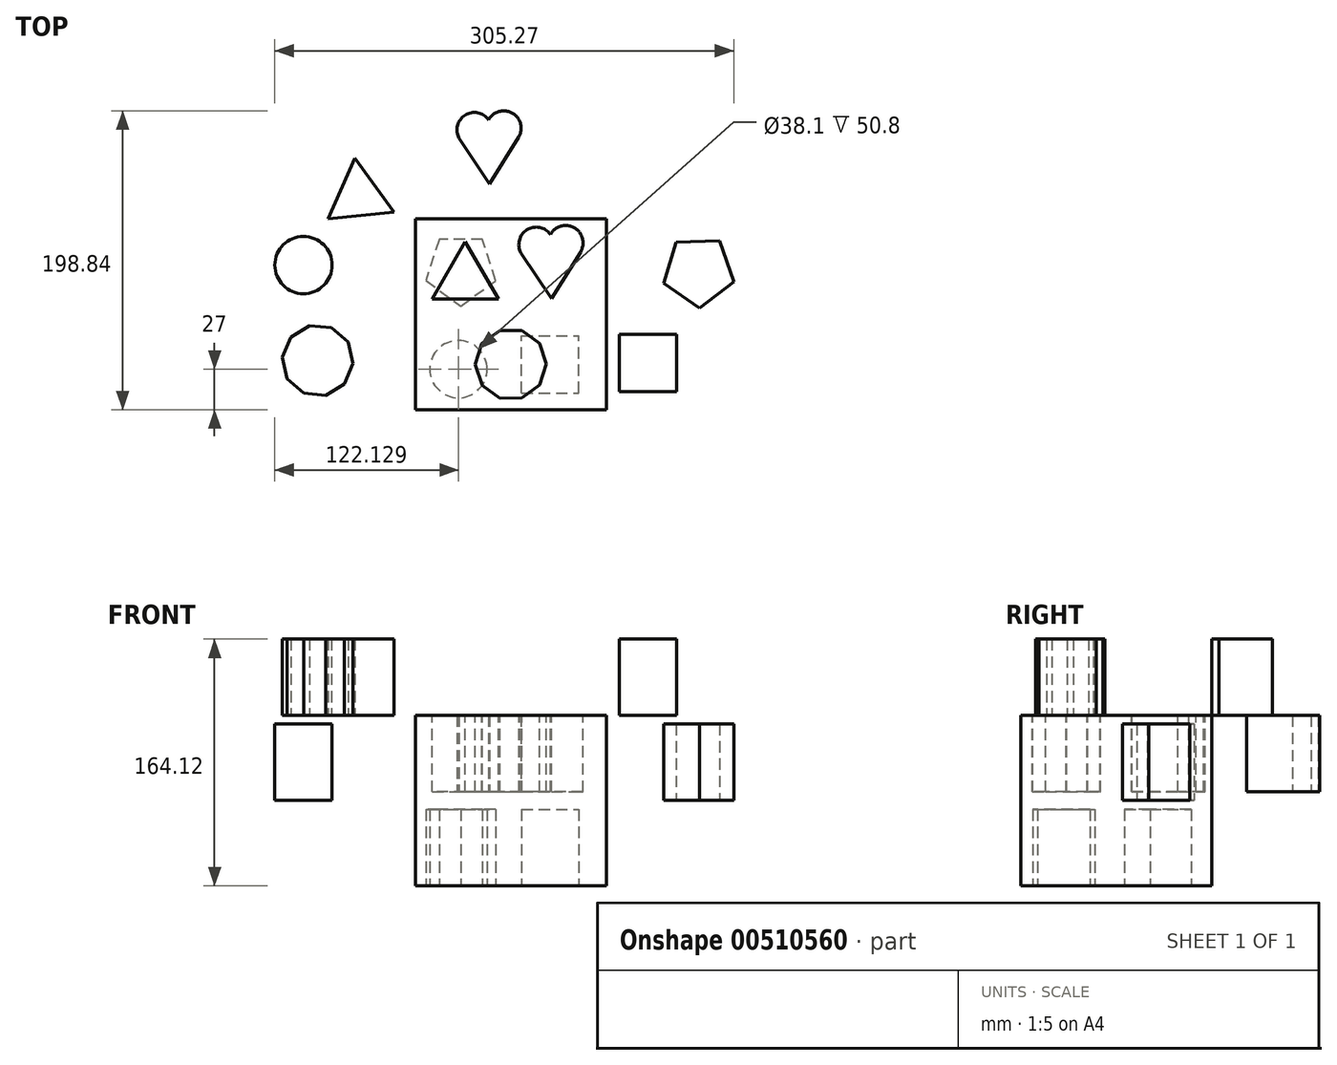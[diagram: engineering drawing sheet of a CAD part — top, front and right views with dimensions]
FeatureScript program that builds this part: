
annotation { "Feature Type Name" : "Feature", "Feature Type Description" : "" }
export const myFeature = defineFeature(function(context is Context, id is Id, definition is map)
    precondition{}
    {
        {
            var Q0;
            Q0=qCreatedBy(makeId("Front.planeOp"),FACE);
            var sketch = newSketch(context, id + "F0", { "sketchPlane" : qUnion([Q0])});
            skLineSegment(sketch, "E0.bottom", {"start": v(-63.3, 56.37) * mm, "end": v(63.7, 56.37) * mm});
            skLineSegment(sketch, "E0.top", {"start": v(-63.3, -56.95) * mm, "end": v(63.7, -56.95) * mm});
            skLineSegment(sketch, "E0.left", {"start": v(-63.3, 56.37) * mm, "end": v(-63.3, -56.95) * mm});
            skLineSegment(sketch, "E0.right", {"start": v(63.7, 56.37) * mm, "end": v(63.7, -56.95) * mm});
            skSolve(sketch);
        }
        {
            var Q0;
            Q0 = qSketchRegion(id + "F0", true);
            extrude(context, id + "F1", {"entities" : qUnion([Q0]), "depth" : 127 * mm});
        }
        {
            var Q0;
            Q0=makeQuery(id+"F1.opExtrude","SWEPT_FACE",FACE,{"disambiguationData":[OSD([sQuery(id+"F0.wireOp",EDGE,"E0.top")])]});
            var sketch = newSketch(context, id + "F2", { "sketchPlane" : qUnion([Q0])});
            skCircle(sketch, "E1", {"center": v(-34.88, 100) * mm, "radius": 19.05 * mm});
            skSolve(sketch);
        }
        {
            var Q0;
            Q0=makeQuery(id+"F2.imprint","IMPRINT",FACE,{"disambiguationData":[TD([[makeQuery(id+"F2.imprint","IMPRINT",EDGE,{"derivedFrom":sQuery(id+"F2.wireOp",EDGE,"E1")}),1.0]])]});
            extrude(context, id + "F3", {"entities" : qUnion([Q0]), "operationType" : NewBodyOperationType.REMOVE, "oppositeDirection" : true, "depth" : 50.8 * mm});
        }
        {
            var Q0;
            Q0=makeQuery(id+"F1.opExtrude","SWEPT_FACE",FACE,{"disambiguationData":[OSD([sQuery(id+"F0.wireOp",EDGE,"E0.top")])]});
            var sketch = newSketch(context, id + "F4", { "sketchPlane" : qUnion([Q0])});
            skLineSegment(sketch, "E2.bottom", {"start": v(7.05, 115.87) * mm, "end": v(45.15, 115.87) * mm});
            skLineSegment(sketch, "E2.top", {"start": v(7.05, 77.77) * mm, "end": v(45.15, 77.77) * mm});
            skLineSegment(sketch, "E2.left", {"start": v(7.05, 115.87) * mm, "end": v(7.05, 77.77) * mm});
            skLineSegment(sketch, "E2.right", {"start": v(45.15, 115.87) * mm, "end": v(45.15, 77.77) * mm});
            skSolve(sketch);
        }
        {
            var Q0;
            Q0=makeQuery(id+"F4.imprint","IMPRINT",FACE,{"disambiguationData":[TD([[makeQuery(id+"F4.imprint","IMPRINT",EDGE,{"derivedFrom":sQuery(id+"F4.wireOp",EDGE,"E2.bottom")}),-1.0]])]});
            extrude(context, id + "F5", {"entities" : qUnion([Q0]), "operationType" : NewBodyOperationType.REMOVE, "oppositeDirection" : true, "depth" : 50.8 * mm});
        }
        {
            var Q0;
            Q0=makeQuery(id+"F1.opExtrude","SWEPT_FACE",FACE,{"disambiguationData":[OSD([sQuery(id+"F0.wireOp",EDGE,"E0.top")])]});
            var sketch = newSketch(context, id + "F6", { "sketchPlane" : qUnion([Q0])});
            skCircle(sketch, "E3.cCircle", {"center": v(-33.35, 33.53) * mm, "radius": 19.77 * mm, "construction": true});
            skLineSegment(sketch, "E3.0", {"start": v(-47.68, 13.73) * mm, "end": v(-56.6, 41.05) * mm});
            skLineSegment(sketch, "E3.1", {"start": v(-56.6, 41.05) * mm, "end": v(-33.38, 57.97) * mm});
            skLineSegment(sketch, "E3.2", {"start": v(-33.38, 57.97) * mm, "end": v(-10.11, 41.12) * mm});
            skLineSegment(sketch, "E3.3", {"start": v(-10.11, 41.12) * mm, "end": v(-18.95, 13.78) * mm});
            skLineSegment(sketch, "E3.4", {"start": v(-18.95, 13.78) * mm, "end": v(-47.68, 13.73) * mm});
            skPoint(sketch, "E3.0.midPoint", {"position": v(-52.14, 27.39) * mm});
            skSolve(sketch);
        }
        {
            var Q0;
            Q0=makeQuery(id+"F6.imprint","IMPRINT",FACE,{"disambiguationData":[TD([[makeQuery(id+"F6.imprint","IMPRINT",EDGE,{"derivedFrom":sQuery(id+"F6.wireOp",EDGE,"E3.0")}),-1.0]])]});
            extrude(context, id + "F7", {"entities" : qUnion([Q0]), "operationType" : NewBodyOperationType.REMOVE, "oppositeDirection" : true, "depth" : 50.8 * mm});
        }
        {
            var Q0;
            Q0=makeQuery(id+"F1.opExtrude","SWEPT_FACE",FACE,{"disambiguationData":[OSD([sQuery(id+"F0.wireOp",EDGE,"E0.bottom")])]});
            var sketch = newSketch(context, id + "F8", { "sketchPlane" : qUnion([Q0])});
            skLineSegment(sketch, "E4", {"start": v(-30.32, -15.29) * mm, "end": v(-52.34, -53.43) * mm});
            skLineSegment(sketch, "E5", {"start": v(-52.34, -53.43) * mm, "end": v(-8.3, -53.43) * mm});
            skLineSegment(sketch, "E6", {"start": v(-8.3, -53.43) * mm, "end": v(-30.32, -15.29) * mm});
            skSolve(sketch);
        }
        {
            var Q0;
            Q0 = qSketchRegion(id + "F8", true);
            extrude(context, id + "F9", {"entities" : qUnion([Q0]), "operationType" : NewBodyOperationType.REMOVE, "oppositeDirection" : true, "depth" : 50.8 * mm});
        }
        {
            var Q0;
            Q0=makeQuery(id+"F1.opExtrude","SWEPT_FACE",FACE,{"disambiguationData":[OSD([sQuery(id+"F0.wireOp",EDGE,"E0.bottom")])]});
            var sketch = newSketch(context, id + "F10", { "sketchPlane" : qUnion([Q0])});
            skLineSegment(sketch, "E7", {"start": v(6.74, -22.72) * mm, "end": v(26.99, -53.15) * mm});
            skLineSegment(sketch, "E8", {"start": v(26.99, -53.15) * mm, "end": v(46.25, -22.08) * mm});
            skArc(sketch, "E9", {"start": v(26.28, -10.36) * mm, "mid": v(10.67, -7.3) * mm, "end": v(6.74, -22.72) * mm});
            skArc(sketch, "E10", {"start": v(46.25, -22.08) * mm, "mid": v(42.27, -6) * mm, "end": v(26.28, -10.36) * mm});
            skPoint(sketch, "E11.orphan", {"position": v(26.99, -22.72) * mm});
            skSolve(sketch);
        }
        {
            var Q0;
            Q0=makeQuery(id+"F10.imprint","IMPRINT",FACE,{"disambiguationData":[TD([[makeQuery(id+"F10.imprint","IMPRINT",EDGE,{"derivedFrom":sQuery(id+"F10.wireOp",EDGE,"E7")}),1.0]])]});
            extrude(context, id + "F11", {"entities" : qUnion([Q0]), "operationType" : NewBodyOperationType.REMOVE, "oppositeDirection" : true, "depth" : 50.8 * mm});
        }
        {
            var Q0;
            Q0=makeQuery(id+"F1.opExtrude","SWEPT_FACE",FACE,{"disambiguationData":[OSD([sQuery(id+"F0.wireOp",EDGE,"E0.bottom")])]});
            var sketch = newSketch(context, id + "F12", { "sketchPlane" : qUnion([Q0])});
            skCircle(sketch, "E12.cCircle", {"center": v(0, -96.69) * mm, "radius": 22.53 * mm, "construction": true});
            skLineSegment(sketch, "E12.0", {"start": v(7.25, -74.14) * mm, "end": v(19.13, -82.7) * mm});
            skLineSegment(sketch, "E12.1", {"start": v(19.13, -82.7) * mm, "end": v(23.7, -96.62) * mm});
            skLineSegment(sketch, "E12.2", {"start": v(23.7, -96.62) * mm, "end": v(19.2, -110.56) * mm});
            skLineSegment(sketch, "E12.3", {"start": v(19.2, -110.56) * mm, "end": v(7.39, -119.2) * mm});
            skLineSegment(sketch, "E12.4", {"start": v(7.39, -119.2) * mm, "end": v(-7.25, -119.24) * mm});
            skLineSegment(sketch, "E12.5", {"start": v(-7.25, -119.24) * mm, "end": v(-19.13, -110.67) * mm});
            skLineSegment(sketch, "E12.6", {"start": v(-19.13, -110.67) * mm, "end": v(-23.7, -96.76) * mm});
            skLineSegment(sketch, "E12.7", {"start": v(-23.7, -96.76) * mm, "end": v(-19.2, -82.82) * mm});
            skLineSegment(sketch, "E12.8", {"start": v(-19.2, -82.82) * mm, "end": v(-7.39, -74.18) * mm});
            skLineSegment(sketch, "E12.9", {"start": v(-7.39, -74.18) * mm, "end": v(7.25, -74.14) * mm});
            skPoint(sketch, "E12.0.midPoint", {"position": v(13.19, -78.42) * mm});
            skSolve(sketch);
        }
        {
            var Q0;
            Q0=makeQuery(id+"F12.imprint","IMPRINT",FACE,{"disambiguationData":[TD([[makeQuery(id+"F12.imprint","IMPRINT",EDGE,{"derivedFrom":sQuery(id+"F12.wireOp",EDGE,"E12.0")}),-1.0]])]});
            extrude(context, id + "F13", {"entities" : qUnion([Q0]), "operationType" : NewBodyOperationType.REMOVE, "oppositeDirection" : true, "depth" : 50.8 * mm});
        }
        {
            var Q0;
            Q0=makeQuery(id+"F1.opExtrude","SWEPT_FACE",FACE,{"disambiguationData":[OSD([sQuery(id+"F0.wireOp",EDGE,"E0.bottom")])]});
            var sketch = newSketch(context, id + "F14", { "sketchPlane" : qUnion([Q0])});
            skLineSegment(sketch, "E13.bottom", {"start": v(72.05, -115.02) * mm, "end": v(110.15, -115.02) * mm});
            skLineSegment(sketch, "E13.top", {"start": v(72.05, -76.92) * mm, "end": v(110.15, -76.92) * mm});
            skLineSegment(sketch, "E13.left", {"start": v(72.05, -115.02) * mm, "end": v(72.05, -76.92) * mm});
            skLineSegment(sketch, "E13.right", {"start": v(110.15, -115.02) * mm, "end": v(110.15, -76.92) * mm});
            skSolve(sketch);
        }
        {
            var Q0;
            Q0=qCreatedBy(makeId("Top.planeOp"),FACE);
            var sketch = newSketch(context, id + "F15", { "sketchPlane" : qUnion([Q0])});
            skCircle(sketch, "E14.cCircle", {"center": v(124.84, -34.83) * mm, "radius": 19.77 * mm, "construction": true});
            skLineSegment(sketch, "E14.0", {"start": v(138.72, -14.71) * mm, "end": v(148.26, -41.81) * mm});
            skLineSegment(sketch, "E14.1", {"start": v(148.26, -41.81) * mm, "end": v(125.44, -59.26) * mm});
            skLineSegment(sketch, "E14.2", {"start": v(125.44, -59.26) * mm, "end": v(101.79, -42.95) * mm});
            skLineSegment(sketch, "E14.3", {"start": v(101.79, -42.95) * mm, "end": v(110, -15.41) * mm});
            skLineSegment(sketch, "E14.4", {"start": v(110, -15.41) * mm, "end": v(138.72, -14.71) * mm});
            skPoint(sketch, "E14.0.midPoint", {"position": v(143.5, -28.26) * mm});
            skSolve(sketch);
        }
        {
            var Q0;
            Q0=qCreatedBy(makeId("Top.planeOp"),FACE);
            var sketch = newSketch(context, id + "F16", { "sketchPlane" : qUnion([Q0])});
            skCircle(sketch, "E15", {"center": v(-137.96, -30.74) * mm, "radius": 19.05 * mm});
            skSolve(sketch);
        }
        {
            var Q0;
            Q0=makeQuery(id+"F16.imprint","IMPRINT",FACE,{"disambiguationData":[TD([[makeQuery(id+"F16.imprint","IMPRINT",EDGE,{"derivedFrom":sQuery(id+"F16.wireOp",EDGE,"E15")}),1.0]])]});
            extrude(context, id + "F17", {"entities" : qUnion([Q0]), "depth" : 50.8 * mm, "offsetDistance" : 25.4 * mm});
        }
        {
            var Q0;
            Q0=makeQuery(id+"F14.imprint","IMPRINT",FACE,{"disambiguationData":[TD([[makeQuery(id+"F14.imprint","IMPRINT",EDGE,{"derivedFrom":sQuery(id+"F14.wireOp",EDGE,"E13.bottom")}),1.0]])]});
            var Q1;
            Q1=makeQuery(id+"F15.imprint","IMPRINT",FACE,{"disambiguationData":[TD([[makeQuery(id+"F15.imprint","IMPRINT",EDGE,{"derivedFrom":sQuery(id+"F15.wireOp",EDGE,"E14.0")}),-1.0]])]});
            extrude(context, id + "F18", {"entities" : qUnion([Q0, Q1]), "depth" : 50.8 * mm, "offsetDistance" : 25.4 * mm});
        }
        {
            var Q0;
            Q0=makeQuery(id+"F1.opExtrude","SWEPT_FACE",FACE,{"disambiguationData":[OSD([sQuery(id+"F0.wireOp",EDGE,"E0.bottom")])]});
            var sketch = newSketch(context, id + "F19", { "sketchPlane" : qUnion([Q0])});
            skPoint(sketch, "E16.0.midPoint", {"position": v(-138.54, -63.3) * mm});
            skCircle(sketch, "E17.cCircle", {"center": v(-128.5, -94.22) * mm, "radius": 22.53 * mm, "construction": true});
            skLineSegment(sketch, "E17.0", {"start": v(-146.36, -78.64) * mm, "end": v(-133.8, -71.12) * mm});
            skLineSegment(sketch, "E17.1", {"start": v(-133.8, -71.12) * mm, "end": v(-119.21, -72.42) * mm});
            skLineSegment(sketch, "E17.2", {"start": v(-119.21, -72.42) * mm, "end": v(-108.18, -82.05) * mm});
            skLineSegment(sketch, "E17.3", {"start": v(-108.18, -82.05) * mm, "end": v(-104.9, -96.32) * mm});
            skLineSegment(sketch, "E17.4", {"start": v(-104.9, -96.32) * mm, "end": v(-110.65, -109.8) * mm});
            skLineSegment(sketch, "E17.5", {"start": v(-110.65, -109.8) * mm, "end": v(-123.21, -117.31) * mm});
            skLineSegment(sketch, "E17.6", {"start": v(-123.21, -117.31) * mm, "end": v(-137.8, -116.01) * mm});
            skLineSegment(sketch, "E17.7", {"start": v(-137.8, -116.01) * mm, "end": v(-148.83, -106.39) * mm});
            skLineSegment(sketch, "E17.8", {"start": v(-148.83, -106.39) * mm, "end": v(-152.1, -92.11) * mm});
            skLineSegment(sketch, "E17.9", {"start": v(-152.1, -92.11) * mm, "end": v(-146.36, -78.64) * mm});
            skPoint(sketch, "E17.0.midPoint", {"position": v(-140.08, -74.88) * mm});
            skSolve(sketch);
        }
        {
            var Q0;
            Q0 = qSketchRegion(id + "F19", true);
            extrude(context, id + "F20", {"entities" : qUnion([Q0]), "depth" : 50.8 * mm, "offsetDistance" : 25.4 * mm});
        }
        {
            var Q0;
            Q0=makeQuery(id+"F1.opExtrude","SWEPT_FACE",FACE,{"disambiguationData":[OSD([sQuery(id+"F0.wireOp",EDGE,"E0.bottom")])]});
            var sketch = newSketch(context, id + "F21", { "sketchPlane" : qUnion([Q0])});
            skLineSegment(sketch, "E18", {"start": v(-103.71, 40.23) * mm, "end": v(-121.64, 0) * mm});
            skLineSegment(sketch, "E19", {"start": v(-121.64, 0) * mm, "end": v(-77.83, 4.59) * mm});
            skLineSegment(sketch, "E20", {"start": v(-77.83, 4.59) * mm, "end": v(-103.71, 40.23) * mm});
            skSolve(sketch);
        }
        {
            var Q0;
            Q0=makeQuery(id+"F21.imprint","IMPRINT",FACE,{"disambiguationData":[TD([[makeQuery(id+"F21.imprint","IMPRINT",EDGE,{"derivedFrom":sQuery(id+"F21.wireOp",EDGE,"E18")}),1.0]])]});
            var Q1;
            Q1=sQuery(id+"F21.wireOp",EDGE,"E20");
            var Q2;
            Q2=sQuery(id+"F21.wireOp",EDGE,"E18");
            var Q3;
            Q3=sQuery(id+"F21.wireOp",EDGE,"E19");
            extrude(context, id + "F22", {"entities" : qUnion([Q0]), "surfaceEntities" : qUnion([Q1, Q2, Q3]), "depth" : 50.8 * mm, "offsetDistance" : 25.4 * mm});
        }
        {
            var Q0;
            Q0=makeQuery(id+"F11.boolean.opBoolean","COPY",FACE,{"derivedFrom":makeQuery(id+"F11.opExtrude","CAP_FACE",FACE,{"disambiguationData":[OSD([sQuery(id+"F10.wireOp",EDGE,"E7"),sQuery(id+"F10.wireOp",EDGE,"E8"),sQuery(id+"F10.wireOp",EDGE,"E9"),sQuery(id+"F10.wireOp",EDGE,"E10")])],"isStart":false})});
            var sketch = newSketch(context, id + "F23", { "sketchPlane" : qUnion([Q0])});
            skLineSegment(sketch, "E21", {"start": v(-34.42, 53.52) * mm, "end": v(-14.17, 23.08) * mm});
            skLineSegment(sketch, "E22", {"start": v(-14.17, 23.08) * mm, "end": v(5.1, 54.15) * mm});
            skArc(sketch, "E23", {"start": v(-14.88, 65.88) * mm, "mid": v(-30.49, 68.93) * mm, "end": v(-34.42, 53.52) * mm});
            skArc(sketch, "E24", {"start": v(5.1, 54.15) * mm, "mid": v(1.11, 70.24) * mm, "end": v(-14.88, 65.88) * mm});
            skPoint(sketch, "E25.orphan", {"position": v(-14.17, 53.52) * mm});
            skSolve(sketch);
        }
        {
            var Q0;
            Q0=makeQuery(id+"F23.imprint","IMPRINT",FACE,{"disambiguationData":[TD([[makeQuery(id+"F23.imprint","IMPRINT",EDGE,{"derivedFrom":sQuery(id+"F23.wireOp",EDGE,"E21")}),1.0]])]});
            var Q1;
            Q1=sQuery(id+"F23.wireOp",EDGE,"E21");
            var Q2;
            Q2=sQuery(id+"F23.wireOp",EDGE,"E23");
            var Q3;
            Q3=sQuery(id+"F23.wireOp",EDGE,"E24");
            var Q4;
            Q4=sQuery(id+"F23.wireOp",EDGE,"E22");
            extrude(context, id + "F24", {"entities" : qUnion([Q0]), "surfaceEntities" : qUnion([Q1, Q2, Q3, Q4]), "depth" : 50.8 * mm, "offsetDistance" : 25.4 * mm});
        }
    });
